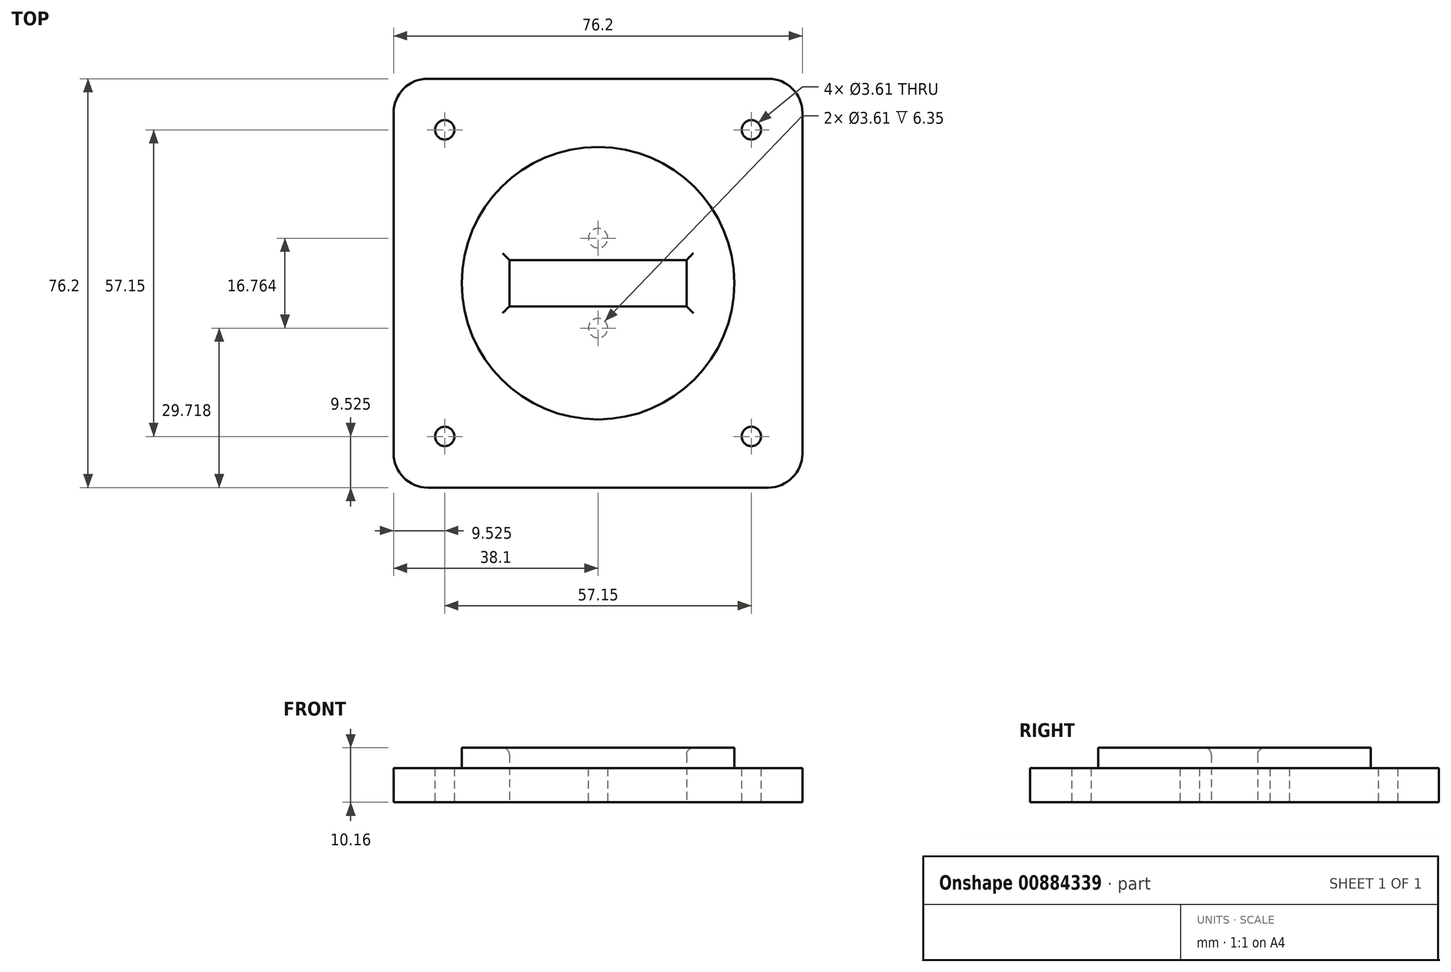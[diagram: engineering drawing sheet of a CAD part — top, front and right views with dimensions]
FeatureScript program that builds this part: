
annotation { "Feature Type Name" : "Feature", "Feature Type Description" : "" }
export const myFeature = defineFeature(function(context is Context, id is Id, definition is map)
    precondition{}
    {
        {
            var Q0;
            Q0=qCreatedBy(makeId("Top.planeOp"),FACE);
            var sketch = newSketch(context, id + "F0", { "sketchPlane" : qUnion([Q0])});
            skPoint(sketch, "E0.middle", {"position": v(0, 0) * mm});
            skCircle(sketch, "E1", {"center": v(0, 0) * mm, "radius": 25.4 * mm});
            skLineSegment(sketch, "E2.bottom", {"start": v(31.75, -38.1) * mm, "end": v(-31.75, -38.1) * mm});
            skLineSegment(sketch, "E2.top", {"start": v(31.75, 38.1) * mm, "end": v(-31.75, 38.1) * mm});
            skLineSegment(sketch, "E2.left", {"start": v(38.1, -31.75) * mm, "end": v(38.1, 31.75) * mm});
            skLineSegment(sketch, "E2.right", {"start": v(-38.1, -31.75) * mm, "end": v(-38.1, 31.75) * mm});
            skPoint(sketch, "E3.visualSharp", {"position": v(-38.1, 38.1) * mm});
            skArc(sketch, "E3.filletArc", {"start": v(-31.75, 38.1) * mm, "mid": v(-36.24, 36.24) * mm, "end": v(-38.1, 31.75) * mm});
            skPoint(sketch, "E4.visualSharp", {"position": v(38.1, 38.1) * mm});
            skArc(sketch, "E4.filletArc", {"start": v(38.1, 31.75) * mm, "mid": v(36.24, 36.24) * mm, "end": v(31.75, 38.1) * mm});
            skPoint(sketch, "E5.visualSharp", {"position": v(38.1, -38.1) * mm});
            skArc(sketch, "E5.filletArc", {"start": v(31.75, -38.1) * mm, "mid": v(36.24, -36.24) * mm, "end": v(38.1, -31.75) * mm});
            skPoint(sketch, "E6.visualSharp", {"position": v(-38.1, -38.1) * mm});
            skArc(sketch, "E6.filletArc", {"start": v(-38.1, -31.75) * mm, "mid": v(-36.24, -36.24) * mm, "end": v(-31.75, -38.1) * mm});
            skCircle(sketch, "E7", {"center": v(-28.57, 28.57) * mm, "radius": 1.8 * mm});
            skCircle(sketch, "E8.0.1.0", {"center": v(-28.57, -28.58) * mm, "radius": 1.8 * mm});
            skCircle(sketch, "E8.1.0.0", {"center": v(28.58, 28.57) * mm, "radius": 1.8 * mm});
            skCircle(sketch, "E8.1.1.0", {"center": v(28.58, -28.58) * mm, "radius": 1.8 * mm});
            skCircle(sketch, "E9", {"center": v(0, 8.38) * mm, "radius": 1.8 * mm});
            skCircle(sketch, "E10.MirrorC", {"center": v(0, -8.38) * mm, "radius": 1.8 * mm});
            skLineSegment(sketch, "E11.bottom", {"start": v(16.51, -4.32) * mm, "end": v(-16.51, -4.32) * mm});
            skLineSegment(sketch, "E11.top", {"start": v(16.51, 4.32) * mm, "end": v(-16.51, 4.32) * mm});
            skLineSegment(sketch, "E11.left", {"start": v(16.51, -4.32) * mm, "end": v(16.51, 4.32) * mm});
            skLineSegment(sketch, "E11.right", {"start": v(-16.51, -4.32) * mm, "end": v(-16.51, 4.32) * mm});
            skSolve(sketch);
        }
        {
            var Q0;
            Q0=qSketchRegion(id+"F0",true);
            var Q1;
            Q1=makeQuery(id+"F0.imprint","IMPRINT",FACE,{"disambiguationData":[TD([[makeQuery(id+"F0.imprint","IMPRINT",EDGE,{"derivedFrom":sQuery(id+"F0.wireOp",EDGE,"bvMOM9Ue-xFAh-koKg-2h8d-dkSVQgIbYXMK")}),-1.0]])]});
            var Q2;
            Q2=makeQuery(id+"F0.imprint","IMPRINT",FACE,{"disambiguationData":[TD([[makeQuery(id+"F0.imprint","IMPRINT",EDGE,{"derivedFrom":sQuery(id+"F0.wireOp",EDGE,"E1")}),1.0]])]});
            extrude(context, id + "F1", {"entities" : qUnion([Q0, Q1, Q2]), "depth" : 6.35 * mm, "offsetDistance" : 25.4 * mm});
        }
        {
            var Q0;
            Q0=makeQuery(id+"F1.opExtrude","CAP_FACE",FACE,{"disambiguationData":[OSD([sQuery(id+"F0.wireOp",EDGE,"bvMOM9Ue-xFAh-koKg-2h8d-dkSVQgIbYXMK"),sQuery(id+"F0.wireOp",EDGE,"wfOdrISR-NwLC-zCM7-E8w8-arZ1y6P3cewp"),sQuery(id+"F0.wireOp",EDGE,"qYbVIByn-fjI4-39u3-IuW1-mppo0c9dRxPc"),sQuery(id+"F0.wireOp",EDGE,"EGcDOHxI-xtcS-q4kI-LQqo-e8Jh6VGGTuC3"),sQuery(id+"F0.wireOp",EDGE,"1sMKuqbc-tQow-f7Pq-o1io-nMGegqhXcjFe"),sQuery(id+"F0.wireOp",EDGE,"E2.bottom"),sQuery(id+"F0.wireOp",EDGE,"E2.top"),sQuery(id+"F0.wireOp",EDGE,"E2.left"),sQuery(id+"F0.wireOp",EDGE,"E2.right"),sQuery(id+"F0.wireOp",EDGE,"E3.filletArc"),sQuery(id+"F0.wireOp",EDGE,"E4.filletArc"),sQuery(id+"F0.wireOp",EDGE,"E5.filletArc"),sQuery(id+"F0.wireOp",EDGE,"E6.filletArc"),sQuery(id+"F0.wireOp",EDGE,"XSsEHeta-U4sv-nlH9-oRWw-j6BDNqyFMGFm"),sQuery(id+"F0.wireOp",EDGE,"fC1IoWxc-lhqW-LEZ1-8md3-mS0RszfKBzjQ"),sQuery(id+"F0.wireOp",EDGE,"b43c0f25-db06-463c-8b56-5aa3c91719830.MirrorCS"),sQuery(id+"F0.wireOp",EDGE,"0da151e6-5ec0-4ebb-85fd-71d94b7c9cec.1.0"),sQuery(id+"F0.wireOp",EDGE,"0da151e6-5ec0-4ebb-85fd-71d94b7c9cec.1.1"),sQuery(id+"F0.wireOp",EDGE,"0da151e6-5ec0-4ebb-85fd-71d94b7c9cec.2.0"),sQuery(id+"F0.wireOp",EDGE,"0da151e6-5ec0-4ebb-85fd-71d94b7c9cec.2.1"),sQuery(id+"F0.wireOp",EDGE,"0da151e6-5ec0-4ebb-85fd-71d94b7c9cec.3.0"),sQuery(id+"F0.wireOp",EDGE,"0da151e6-5ec0-4ebb-85fd-71d94b7c9cec.3.1"),sQuery(id+"F0.wireOp",EDGE,"0da151e6-5ec0-4ebb-85fd-71d94b7c9cec.4.0"),sQuery(id+"F0.wireOp",EDGE,"0da151e6-5ec0-4ebb-85fd-71d94b7c9cec.4.1"),sQuery(id+"F0.wireOp",EDGE,"01d92755-4c2a-428b-ab72-bc29c4ff26a2.trimOffspring"),sQuery(id+"F0.wireOp",EDGE,"9721003d-029a-4cdd-bbaf-c882f096c370.trimOffspring"),sQuery(id+"F0.wireOp",EDGE,"2a0f4c4f-a360-4e1f-b22d-773e85cdc3bc.trimOffspring"),sQuery(id+"F0.wireOp",EDGE,"f4b1477b-afbf-4256-80e9-cedfa79630e7.trimOffspring"),sQuery(id+"F0.wireOp",EDGE,"3da056b4-4071-4d28-9965-5f42ac81589b.trimOffspring"),sQuery(id+"F0.wireOp",EDGE,"7208ba10-4293-43cf-a357-1ba41f53954b.trimOffspring"),sQuery(id+"F0.wireOp",EDGE,"553c1946-a41b-41c0-8b76-556953ba413b.trimOffspring"),sQuery(id+"F0.wireOp",EDGE,"3e11bdf3-eaaf-42bd-a6a7-7acec3c7161e.trimOffspring"),sQuery(id+"F0.wireOp",EDGE,"E7"),sQuery(id+"F0.wireOp",EDGE,"E8.0.1.0"),sQuery(id+"F0.wireOp",EDGE,"E8.1.0.0"),sQuery(id+"F0.wireOp",EDGE,"E8.1.1.0")])],"isStart":false});
            var sketch = newSketch(context, id + "F2", { "sketchPlane" : qUnion([Q0])});
            skCircle(sketch, "E12", {"center": v(0, 0) * mm, "radius": 25.4 * mm});
            skSolve(sketch);
        }
        {
            var Q0;
            Q0=qSketchRegion(id+"F2",true);
            extrude(context, id + "F3", {"entities" : qUnion([Q0]), "operationType" : NewBodyOperationType.ADD, "depth" : 3.8 * mm, "offsetDistance" : 25.4 * mm});
        }
        {
            var Q0;
            Q0=makeQuery(id+"F0.imprint","IMPRINT",FACE,{"disambiguationData":[TD([[makeQuery(id+"F0.imprint","IMPRINT",EDGE,{"derivedFrom":sQuery(id+"F0.wireOp",EDGE,"E11.bottom")}),-1.0]])]});
            extrude(context, id + "F4", {"entities" : qUnion([Q0]), "operationType" : NewBodyOperationType.REMOVE, "endBound" : BoundingType.SYMMETRIC, "oppositeDirection" : true, "depth" : 25.4 * mm, "offsetDistance" : 25.4 * mm});
        }
        {
            var Q0;
            Q0=makeQuery(id+"F4.boolean.opBoolean","INTERSECT",EDGE,{"derivedFrom":[makeQuery(id+"F3.opExtrude","CAP_FACE",FACE,{"disambiguationData":[OSD([sQuery(id+"F2.wireOp",EDGE,"E12")])],"isStart":false}),makeQuery(id+"F4.opExtrude","SWEPT_FACE",FACE,{"disambiguationData":[OSD([sQuery(id+"F0.wireOp",EDGE,"E11.top")])]})]});
            var Q1;
            Q1=makeQuery(id+"F4.boolean.opBoolean","INTERSECT",EDGE,{"derivedFrom":[makeQuery(id+"F3.opExtrude","CAP_FACE",FACE,{"disambiguationData":[OSD([sQuery(id+"F2.wireOp",EDGE,"E12")])],"isStart":false}),makeQuery(id+"F4.opExtrude","SWEPT_FACE",FACE,{"disambiguationData":[OSD([sQuery(id+"F0.wireOp",EDGE,"E11.right")])]})]});
            var Q2;
            Q2=makeQuery(id+"F4.boolean.opBoolean","INTERSECT",EDGE,{"derivedFrom":[makeQuery(id+"F3.opExtrude","CAP_FACE",FACE,{"disambiguationData":[OSD([sQuery(id+"F2.wireOp",EDGE,"E12")])],"isStart":false}),makeQuery(id+"F4.opExtrude","SWEPT_FACE",FACE,{"disambiguationData":[OSD([sQuery(id+"F0.wireOp",EDGE,"E11.bottom")])]})]});
            var Q3;
            Q3=makeQuery(id+"F4.boolean.opBoolean","INTERSECT",EDGE,{"derivedFrom":[makeQuery(id+"F3.opExtrude","CAP_FACE",FACE,{"disambiguationData":[OSD([sQuery(id+"F2.wireOp",EDGE,"E12")])],"isStart":false}),makeQuery(id+"F4.opExtrude","SWEPT_FACE",FACE,{"disambiguationData":[OSD([sQuery(id+"F0.wireOp",EDGE,"E11.left")])]})]});
            fillet(context, id + "F5", {"entities" : qUnion([Q0, Q1, Q2, Q3]), "radius" : 1.27 * mm, "tangentPropagation" : true, "allowEdgeOverflow" : false});
        }
    });
